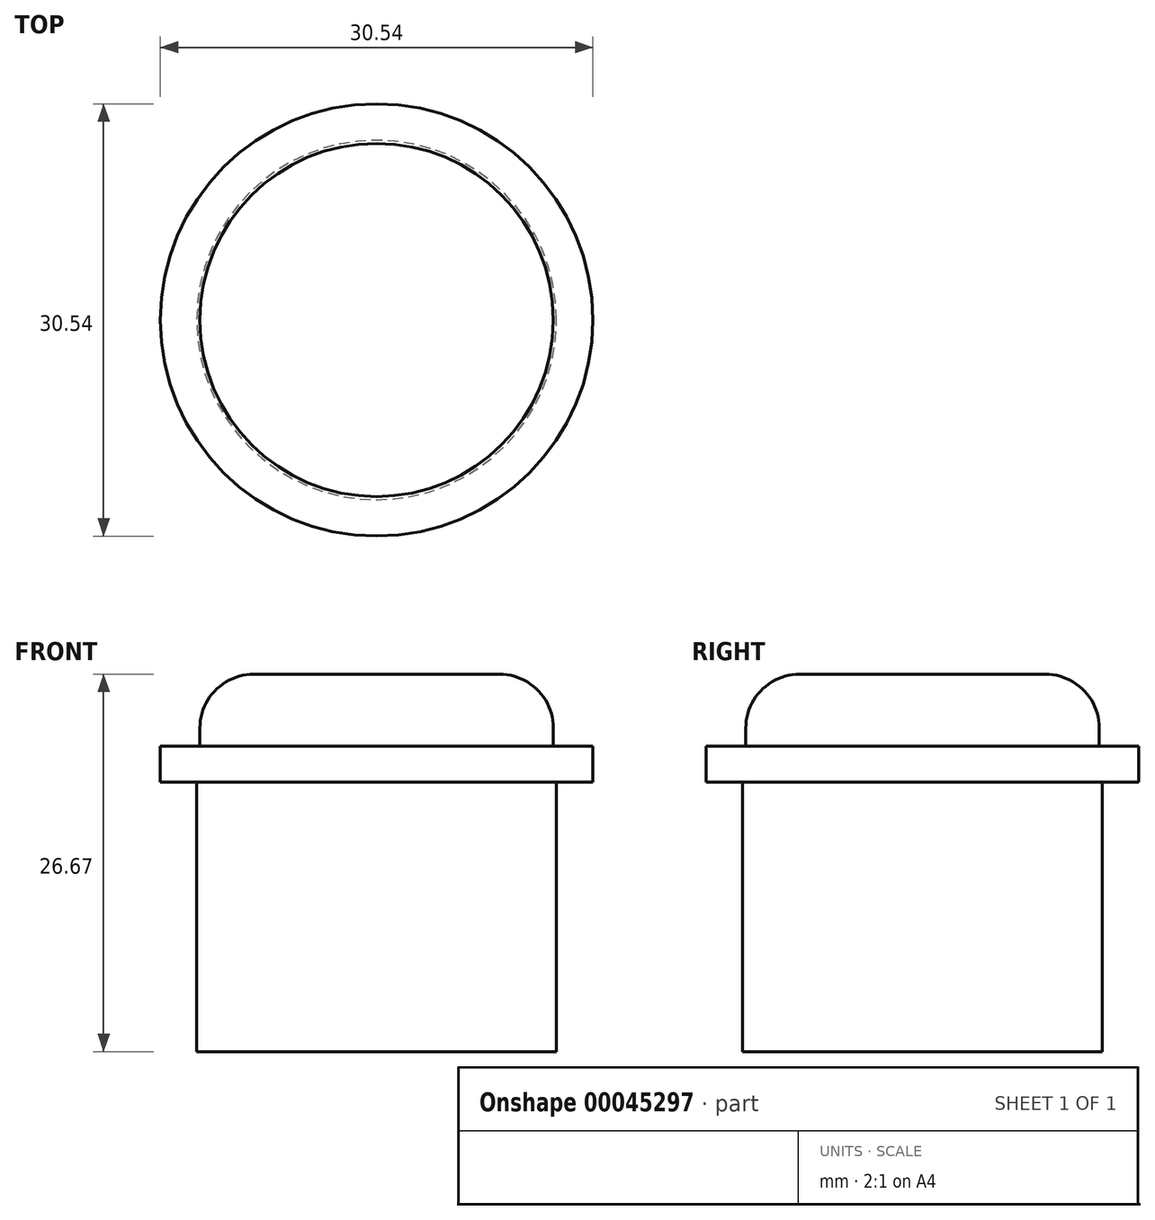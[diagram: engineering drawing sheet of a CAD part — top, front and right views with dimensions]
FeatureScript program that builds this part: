
annotation { "Feature Type Name" : "Feature", "Feature Type Description" : "" }
export const myFeature = defineFeature(function(context is Context, id is Id, definition is map)
    precondition{}
    {
        {
            var Q0;
            Q0=qCreatedBy(makeId("Top.planeOp"),FACE);
            var sketch = newSketch(context, id + "F0", { "sketchPlane" : qUnion([Q0])});
            skCircle(sketch, "E0", {"center": v(0, 0) * mm, "radius": 12.7 * mm});
            skSolve(sketch);
        }
        {
            var Q0;
            Q0=makeQuery(id+"F0.imprint","IMPRINT",FACE,{"disambiguationData":[TD([[makeQuery(id+"F0.imprint","IMPRINT",EDGE,{"derivedFrom":sQuery(id+"F0.wireOp",EDGE,"E0")}),1.0]])]});
            extrude(context, id + "F1", {"entities" : qUnion([Q0]), "depth" : 19.05 * mm});
        }
        {
            var Q0;
            Q0=makeQuery(id+"F1.opExtrude","CAP_FACE",FACE,{"disambiguationData":[OSD([sQuery(id+"F0.wireOp",EDGE,"E0")])],"isStart":false});
            var sketch = newSketch(context, id + "F2", { "sketchPlane" : qUnion([Q0])});
            skCircle(sketch, "E1", {"center": v(0, 0) * mm, "radius": 15.27 * mm});
            skSolve(sketch);
        }
        {
            var Q0;
            Q0=makeQuery(id+"F2.imprint","IMPRINT",FACE,{"disambiguationData":[TD([[makeQuery(id+"F2.imprint","IMPRINT",EDGE,{"derivedFrom":makeQuery(id+"F1.opExtrude","CAP_EDGE",EDGE,{"disambiguationData":[OSD([sQuery(id+"F0.wireOp",EDGE,"E0")])],"isStart":false})}),1.0]])]});
            var Q1;
            Q1=makeQuery(id+"F2.imprint","IMPRINT",FACE,{"disambiguationData":[TD([[makeQuery(id+"F2.imprint","IMPRINT",EDGE,{"derivedFrom":sQuery(id+"F2.wireOp",EDGE,"E1")}),1.0]])]});
            extrude(context, id + "F3", {"entities" : qUnion([Q0, Q1]), "operationType" : NewBodyOperationType.ADD, "depth" : 2.54 * mm});
        }
        {
            var Q0;
            Q0=makeQuery(id+"F3.opExtrude","CAP_FACE",FACE,{"disambiguationData":[OSD([sQuery(id+"F2.wireOp",EDGE,"E1")])],"isStart":false});
            var sketch = newSketch(context, id + "F4", { "sketchPlane" : qUnion([Q0])});
            skCircle(sketch, "E2", {"center": v(0, 0) * mm, "radius": 12.48 * mm});
            skSolve(sketch);
        }
        {
            var Q0;
            Q0=makeQuery(id+"F4.imprint","IMPRINT",FACE,{"disambiguationData":[TD([[makeQuery(id+"F4.imprint","IMPRINT",EDGE,{"derivedFrom":sQuery(id+"F4.wireOp",EDGE,"E2")}),1.0]])]});
            extrude(context, id + "F5", {"entities" : qUnion([Q0]), "operationType" : NewBodyOperationType.ADD, "depth" : 5.08 * mm});
        }
        {
            var Q0;
            Q0=makeQuery(id+"F5.opExtrude","CAP_FACE",FACE,{"disambiguationData":[OSD([sQuery(id+"F4.wireOp",EDGE,"E2")])],"isStart":false});
            fillet(context, id + "F6", {"entities" : qUnion([Q0]), "radius" : 3.8 * mm, "tangentPropagation" : true, "allowEdgeOverflow" : false});
        }
    });
